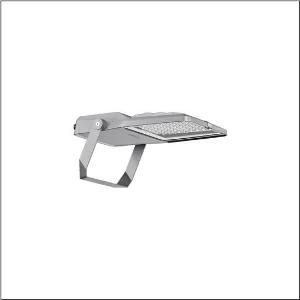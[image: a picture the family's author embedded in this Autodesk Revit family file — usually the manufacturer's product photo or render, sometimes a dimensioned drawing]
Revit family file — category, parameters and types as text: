
# Revit family: floodlight_fl_21_mini___pl61_5xa7775c2c1a_7daf
name_source: partatom
category: Lighting Fixtures
units: mm (PartAtom-declared; Revit-internal decimal feet)

## family parameters
Cut with Voids When Loaded = No
Host = Face
Light Source = No
Part Type = Normal
Room Calculation Point = No
Round Connector Dimension = Use Diameter
Shared = No

## types (1)
- --- (1 x LED, 11960 lm, 89 W, 3000K)
    Apparent Load = 89 VA
    CIE Flux Codes = 33 65 98 100 100
    Color Rendering = 70
    Color Temperature = 3000K
    Default Elevation = 1800 mm
    Description = Floodlight FL 21 mini, floodlight, primary light control with lens, of PMMA, primary optical cover: protective disc, of toughened safety glass, transparent, light distribution: PL61, light emission: direct distribution, installation type: surface-mounted, LED, High Power LED, rated luminous flux: 11.960lm, luminous efficacy: 134lm/W, light colour: 730, colour temperature: 3000K, control: flexible luminous flux parameterisation, time-dependent luminous flux control, constant luminous flux control, overheat protection, presetting dimming logarithmic, with terminal, 6-pole, mains connection: 220..240V, AC, 50/60Hz, start of lifetime: 89W, end of service life: 94W, reduction: 43W, luminaire housing, of diecast aluminium, powder-coated, Siteco® metallic grey (DB 702S), corrosivity category C5 mid according to DIN EN ISO 12944, sealing non-destructively replaceable, mounting bracket, of steel, galvanised, powder-coated, Siteco® metallic grey (DB 702S), Smart Interface above, protection rating (complete): IP66, insulation class (complete): insulation class II (safety insulation), certification: CE, ENEC, VDE, protection symbol: D, impact resistance: IK08, permissible operating ambient temperature: -40..+40°C, permissible operating ambient temperature for outdoor applications: -40..+50°C, standard: DIN EN 12944, LABS conformity tested according to VDMA 24364:2018-05, packaging unit: 1 piece

Light Distribution: PL61
    Height = 70 mm
    Lamp = 1 x LED
    Lamp Light Flux = 11960 lm
    Lamp Power = 89 W
    Lamp count = 1
    Length = 485 mm
    Luminous efficacy = 134 lm/W
    Manufacturer = Siteco
    ModVariant = No
    Model = 5XA7775C2C1A
    Number of Poles = 1
    OnlyDefault = Yes
    Power Factor = 1
    Product Name = Floodlight FL 21 mini | PL61
    Product group = floodlight | pylon annexe
    ProductGroupID = 6200
    Protection Class = Protection class II
    Protection Degree = IP 66
    RLX_Detail_Level = 1
    RLX_Emergency_Light_Flux = 0 lm
    RLX_Emergency_Type = 0
    RLX_Emergency_Type_DB = No
    RlxData = <blob elided: 95765 chars, md5=1da6c9f8>
    Socket = socket
    Standby Power = 0 W
    System Light Flux = 11960 lm
    System Power = 89 W
    Type Comments = factory setting: luminous flux: 100 % | dim-lin: 254 | 456 mA
    Type Image = l_1006845.jpg
    URL = http://relux.com
    VarID = @adj_123021
    Voltage = 0 V
    Weight = 0.00 kg
    Width = 337 mm

## geometry (parser evidence)
native form markers: Blend x4, Sweep x14
no freeform markers — native parametric forms only
